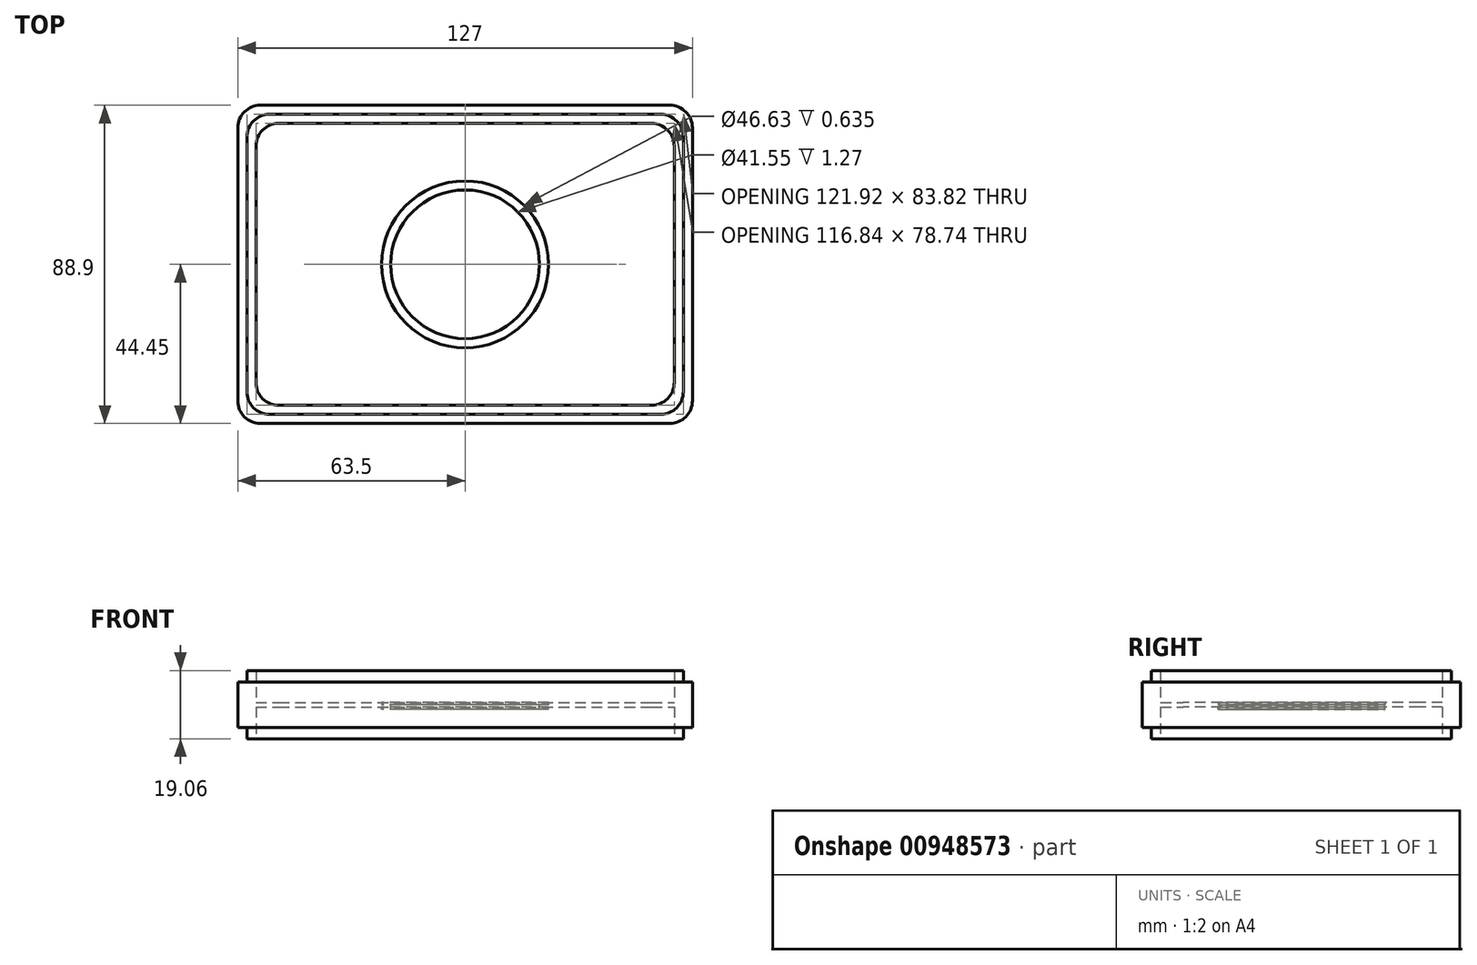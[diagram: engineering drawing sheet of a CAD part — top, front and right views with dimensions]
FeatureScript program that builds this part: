
annotation { "Feature Type Name" : "Feature", "Feature Type Description" : "" }
export const myFeature = defineFeature(function(context is Context, id is Id, definition is map)
    precondition{}
    {
        {
            var Q0;
            Q0=qCreatedBy(makeId("Top.planeOp"),FACE);
            var sketch = newSketch(context, id + "F0", { "sketchPlane" : qUnion([Q0])});
            skLineSegment(sketch, "E0.bottom", {"start": v(-57.15, 44.45) * mm, "end": v(57.15, 44.45) * mm});
            skLineSegment(sketch, "E0.top", {"start": v(-57.15, -44.45) * mm, "end": v(57.15, -44.45) * mm});
            skLineSegment(sketch, "E0.left", {"start": v(-63.5, 38.1) * mm, "end": v(-63.5, -38.1) * mm});
            skLineSegment(sketch, "E0.right", {"start": v(63.5, 38.1) * mm, "end": v(63.5, -38.1) * mm});
            skPoint(sketch, "E0.middle", {"position": v(0, 0) * mm});
            skLineSegment(sketch, "E1.bottom", {"start": v(-54.6, -41.91) * mm, "end": v(54.6, -41.91) * mm});
            skLineSegment(sketch, "E1.top", {"start": v(-54.6, 41.91) * mm, "end": v(54.6, 41.91) * mm});
            skLineSegment(sketch, "E1.left", {"start": v(-60.96, -35.56) * mm, "end": v(-60.96, 35.56) * mm});
            skLineSegment(sketch, "E1.right", {"start": v(60.96, -35.56) * mm, "end": v(60.96, 35.56) * mm});
            skPoint(sketch, "E2.visualSharp", {"position": v(-63.5, 44.45) * mm});
            skArc(sketch, "E2.filletArc", {"start": v(-57.15, 44.45) * mm, "mid": v(-61.64, 42.6) * mm, "end": v(-63.5, 38.1) * mm});
            skPoint(sketch, "E3.visualSharp", {"position": v(63.5, 44.45) * mm});
            skArc(sketch, "E3.filletArc", {"start": v(63.5, 38.1) * mm, "mid": v(61.64, 42.6) * mm, "end": v(57.15, 44.45) * mm});
            skPoint(sketch, "E4.visualSharp", {"position": v(63.5, -44.45) * mm});
            skArc(sketch, "E4.filletArc", {"start": v(57.15, -44.45) * mm, "mid": v(61.64, -42.6) * mm, "end": v(63.5, -38.1) * mm});
            skPoint(sketch, "E5.visualSharp", {"position": v(60.96, -41.91) * mm});
            skArc(sketch, "E5.filletArc", {"start": v(54.6, -41.91) * mm, "mid": v(59.1, -40.05) * mm, "end": v(60.96, -35.56) * mm});
            skPoint(sketch, "E6.visualSharp", {"position": v(60.96, 41.91) * mm});
            skArc(sketch, "E6.filletArc", {"start": v(60.96, 35.56) * mm, "mid": v(59.1, 40.05) * mm, "end": v(54.6, 41.91) * mm});
            skPoint(sketch, "E7.visualSharp", {"position": v(-60.96, -41.91) * mm});
            skArc(sketch, "E7.filletArc", {"start": v(-60.96, -35.56) * mm, "mid": v(-59.1, -40.05) * mm, "end": v(-54.6, -41.91) * mm});
            skPoint(sketch, "E8.visualSharp", {"position": v(-60.96, 41.91) * mm});
            skArc(sketch, "E8.filletArc", {"start": v(-54.6, 41.91) * mm, "mid": v(-59.1, 40.05) * mm, "end": v(-60.96, 35.56) * mm});
            skPoint(sketch, "E9.visualSharp", {"position": v(-63.5, -44.45) * mm});
            skArc(sketch, "E9.filletArc", {"start": v(-63.5, -38.1) * mm, "mid": v(-61.64, -42.6) * mm, "end": v(-57.15, -44.45) * mm});
            skCircle(sketch, "E10", {"center": v(0, 0) * mm, "radius": 20.78 * mm});
            skLineSegment(sketch, "E11.bottom", {"start": v(-52.07, 39.37) * mm, "end": v(52.07, 39.37) * mm});
            skLineSegment(sketch, "E11.top", {"start": v(-52.07, -39.37) * mm, "end": v(52.07, -39.37) * mm});
            skLineSegment(sketch, "E11.left", {"start": v(-58.42, 33.02) * mm, "end": v(-58.42, -33.02) * mm});
            skLineSegment(sketch, "E11.right", {"start": v(58.42, 33.02) * mm, "end": v(58.42, -33.02) * mm});
            skPoint(sketch, "E12.visualSharp", {"position": v(58.42, 39.37) * mm});
            skArc(sketch, "E12.filletArc", {"start": v(58.42, 33.02) * mm, "mid": v(56.56, 37.51) * mm, "end": v(52.07, 39.37) * mm});
            skPoint(sketch, "E13.visualSharp", {"position": v(-58.42, -39.37) * mm});
            skArc(sketch, "E13.filletArc", {"start": v(-58.42, -33.02) * mm, "mid": v(-56.56, -37.51) * mm, "end": v(-52.07, -39.37) * mm});
            skPoint(sketch, "E14.visualSharp", {"position": v(58.42, -39.37) * mm});
            skArc(sketch, "E14.filletArc", {"start": v(52.07, -39.37) * mm, "mid": v(56.56, -37.51) * mm, "end": v(58.42, -33.02) * mm});
            skPoint(sketch, "E15.visualSharp", {"position": v(-58.42, 39.37) * mm});
            skArc(sketch, "E15.filletArc", {"start": v(-52.07, 39.37) * mm, "mid": v(-56.56, 37.51) * mm, "end": v(-58.42, 33.02) * mm});
            skCircle(sketch, "E16", {"center": v(0, 0) * mm, "radius": 23.32 * mm});
            skSolve(sketch);
        }
        {
            var Q0;
            Q0=makeQuery(id+"F0.imprint","IMPRINT",FACE,{"disambiguationData":[TD([[makeQuery(id+"F0.imprint","IMPRINT",EDGE,{"derivedFrom":sQuery(id+"F0.wireOp",EDGE,"E0.bottom")}),-1.0]])]});
            extrude(context, id + "F1", {"entities" : qUnion([Q0]), "endBound" : BoundingType.SYMMETRIC, "depth" : 12.7 * mm, "offsetDistance" : 25.4 * mm});
        }
        {
            var Q0;
            Q0=makeQuery(id+"F0.imprint","IMPRINT",FACE,{"disambiguationData":[TD([[makeQuery(id+"F0.imprint","IMPRINT",EDGE,{"derivedFrom":sQuery(id+"F0.wireOp",EDGE,"E1.bottom")}),1.0]])]});
            extrude(context, id + "F2", {"entities" : qUnion([Q0]), "operationType" : NewBodyOperationType.ADD, "endBound" : BoundingType.SYMMETRIC, "depth" : 19.05 * mm, "offsetDistance" : 25.4 * mm});
        }
        {
            var Q0;
            Q0=makeQuery(id+"F0.imprint","IMPRINT",FACE,{"disambiguationData":[TD([[makeQuery(id+"F0.imprint","IMPRINT",EDGE,{"derivedFrom":sQuery(id+"F0.wireOp",EDGE,"E11.bottom")}),-1.0]])]});
            extrude(context, id + "F3", {"entities" : qUnion([Q0]), "operationType" : NewBodyOperationType.ADD, "endBound" : BoundingType.SYMMETRIC, "depth" : 1.27 * mm, "offsetDistance" : 25.4 * mm});
        }
        {
            var Q0;
            Q0=makeQuery(id+"F0.imprint","IMPRINT",FACE,{"disambiguationData":[TD([[makeQuery(id+"F0.imprint","IMPRINT",EDGE,{"derivedFrom":sQuery(id+"F0.wireOp",EDGE,"E10")}),-1.0]])]});
            extrude(context, id + "F4", {"entities" : qUnion([Q0]), "operationType" : NewBodyOperationType.ADD, "oppositeDirection" : true, "depth" : 1.27 * mm, "offsetDistance" : 25.4 * mm});
        }
    });
